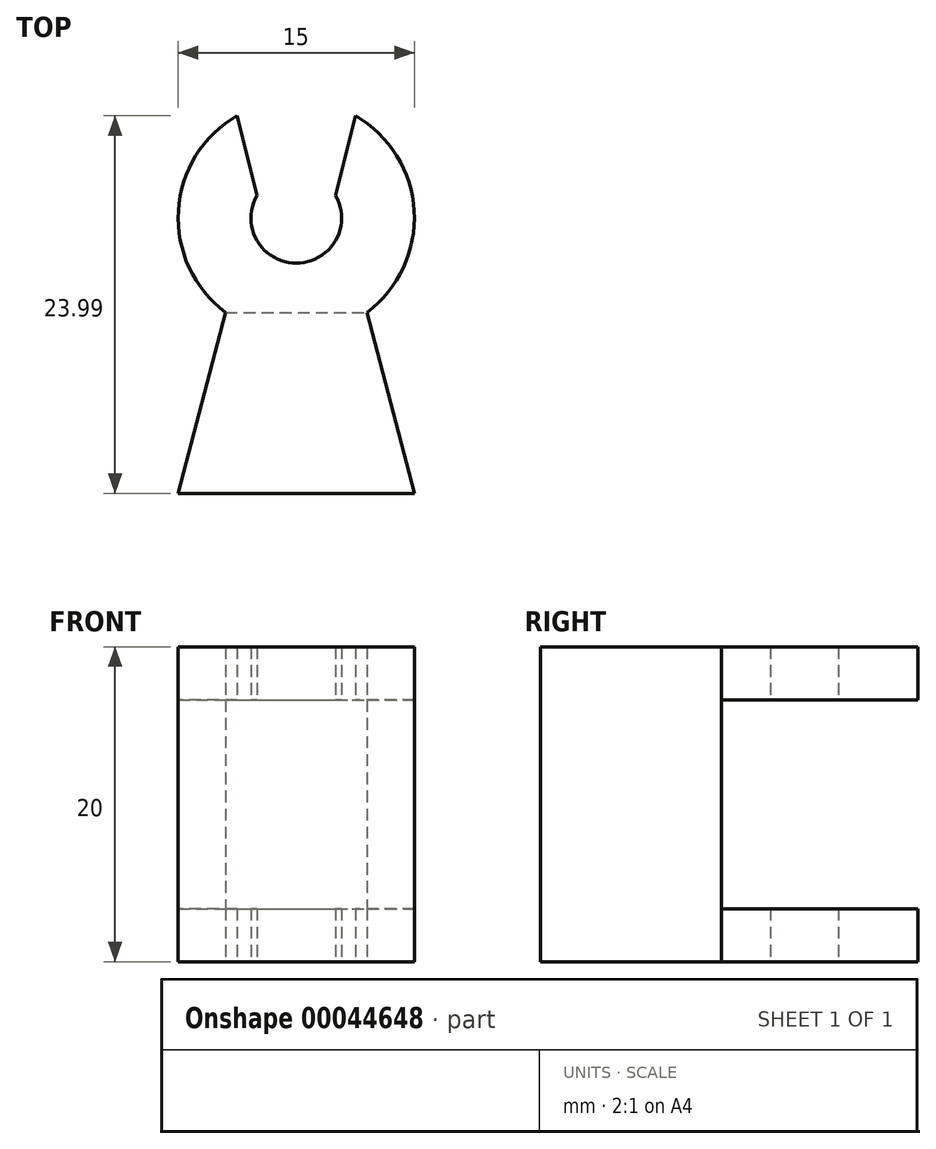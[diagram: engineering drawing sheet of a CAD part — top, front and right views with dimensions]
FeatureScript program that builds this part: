
annotation { "Feature Type Name" : "Feature", "Feature Type Description" : "" }
export const myFeature = defineFeature(function(context is Context, id is Id, definition is map)
    precondition{}
    {
        {
            var Q0;
            Q0=qCreatedBy(makeId("Top.planeOp"),FACE);
            var sketch = newSketch(context, id + "F0", { "sketchPlane" : qUnion([Q0])});
            skLineSegment(sketch, "E0.bottom", {"start": v(-15, 22.15) * mm, "end": v(0, 22.15) * mm});
            skLineSegment(sketch, "E0.top", {"start": v(-15, -2.85) * mm, "end": v(0, -2.85) * mm});
            skLineSegment(sketch, "E0.left", {"start": v(-15, 22.15) * mm, "end": v(-15, -2.85) * mm});
            skLineSegment(sketch, "E0.right", {"start": v(0, 22.15) * mm, "end": v(0, -2.85) * mm});
            skCircle(sketch, "E1", {"center": v(-7.5, 14.65) * mm, "radius": 7.5 * mm});
            skCircle(sketch, "E2", {"center": v(-7.5, 14.65) * mm, "radius": 2.88 * mm});
            skLineSegment(sketch, "E3", {"start": v(0, 22.15) * mm, "end": v(-3.5, 22.15) * mm});
            skLineSegment(sketch, "E4", {"start": v(-15, 22.15) * mm, "end": v(-11.5, 22.15) * mm});
            skLineSegment(sketch, "E5", {"start": v(-10, 16.07) * mm, "end": v(-5, 16.07) * mm});
            skLineSegment(sketch, "E6", {"start": v(-5, 16.07) * mm, "end": v(-3.5, 22.15) * mm});
            skLineSegment(sketch, "E7", {"start": v(-11.5, 22.15) * mm, "end": v(-10, 16.07) * mm});
            skLineSegment(sketch, "E8", {"start": v(-12, 8.65) * mm, "end": v(-3, 8.65) * mm});
            skLineSegment(sketch, "E9", {"start": v(-15, -2.85) * mm, "end": v(-12, 8.65) * mm});
            skLineSegment(sketch, "E10", {"start": v(0, -2.85) * mm, "end": v(-3, 8.65) * mm});
            skSolve(sketch);
        }
        {
            var Q0;
            {var subQ1=sQuery(id+"F0.wireOp",EDGE,"E1");var subQ8=makeQuery(id+"F0.imprint","INTERSECT",VERTEX,{"derivedFrom":[sQuery(id+"F0.wireOp",EDGE,"E0.right"),subQ1]});Q0=makeQuery(id+"F0.imprint","IMPRINT",FACE,{"disambiguationData":[TD([[makeQuery(id+"F0.imprint","IMPRINT",EDGE,{"disambiguationData":[TD([[subQ8,-1.0]])],"derivedFrom":subQ1}),1.0]])]});}
            var Q1;
            {var subQ5=sQuery(id+"F0.wireOp",EDGE,"E0.top");Q1=makeQuery(id+"F0.imprint","IMPRINT",FACE,{"disambiguationData":[TD([[makeQuery(id+"F0.imprint","IMPRINT",EDGE,{"derivedFrom":subQ5}),1.0]])]});}
            var Q2;
            {var subQ0=sQuery(id+"F0.wireOp",EDGE,"E8");Q2=makeQuery(id+"F0.imprint","IMPRINT",FACE,{"disambiguationData":[TD([[makeQuery(id+"F0.imprint","IMPRINT",EDGE,{"derivedFrom":subQ0}),-1.0]])]});}
            extrude(context, id + "F1", {"entities" : qUnion([Q0, Q1, Q2]), "depth" : 20 * mm});
        }
        {
            var Q0;
            {var subQ1=sQuery(id+"F0.wireOp",EDGE,"E1");var subQ8=makeQuery(id+"F0.imprint","INTERSECT",VERTEX,{"derivedFrom":[sQuery(id+"F0.wireOp",EDGE,"E0.right"),subQ1]});Q0=makeQuery(id+"F0.imprint","IMPRINT",FACE,{"disambiguationData":[TD([[makeQuery(id+"F0.imprint","IMPRINT",EDGE,{"disambiguationData":[TD([[subQ8,-1.0]])],"derivedFrom":subQ1}),1.0]])]});}
            extrude(context, id + "F2", {"entities" : qUnion([Q0]), "operationType" : NewBodyOperationType.REMOVE, "depth" : 16.62 * mm});
        }
        {
            var Q0;
            {var subQ1=sQuery(id+"F0.wireOp",EDGE,"E1");var subQ8=makeQuery(id+"F0.imprint","INTERSECT",VERTEX,{"derivedFrom":[sQuery(id+"F0.wireOp",EDGE,"E0.right"),subQ1]});Q0=makeQuery(id+"F0.imprint","IMPRINT",FACE,{"disambiguationData":[TD([[makeQuery(id+"F0.imprint","IMPRINT",EDGE,{"disambiguationData":[TD([[subQ8,-1.0]])],"derivedFrom":subQ1}),1.0]])]});}
            extrude(context, id + "F3", {"entities" : qUnion([Q0]), "operationType" : NewBodyOperationType.ADD, "depth" : 3.38 * mm});
        }
    });
